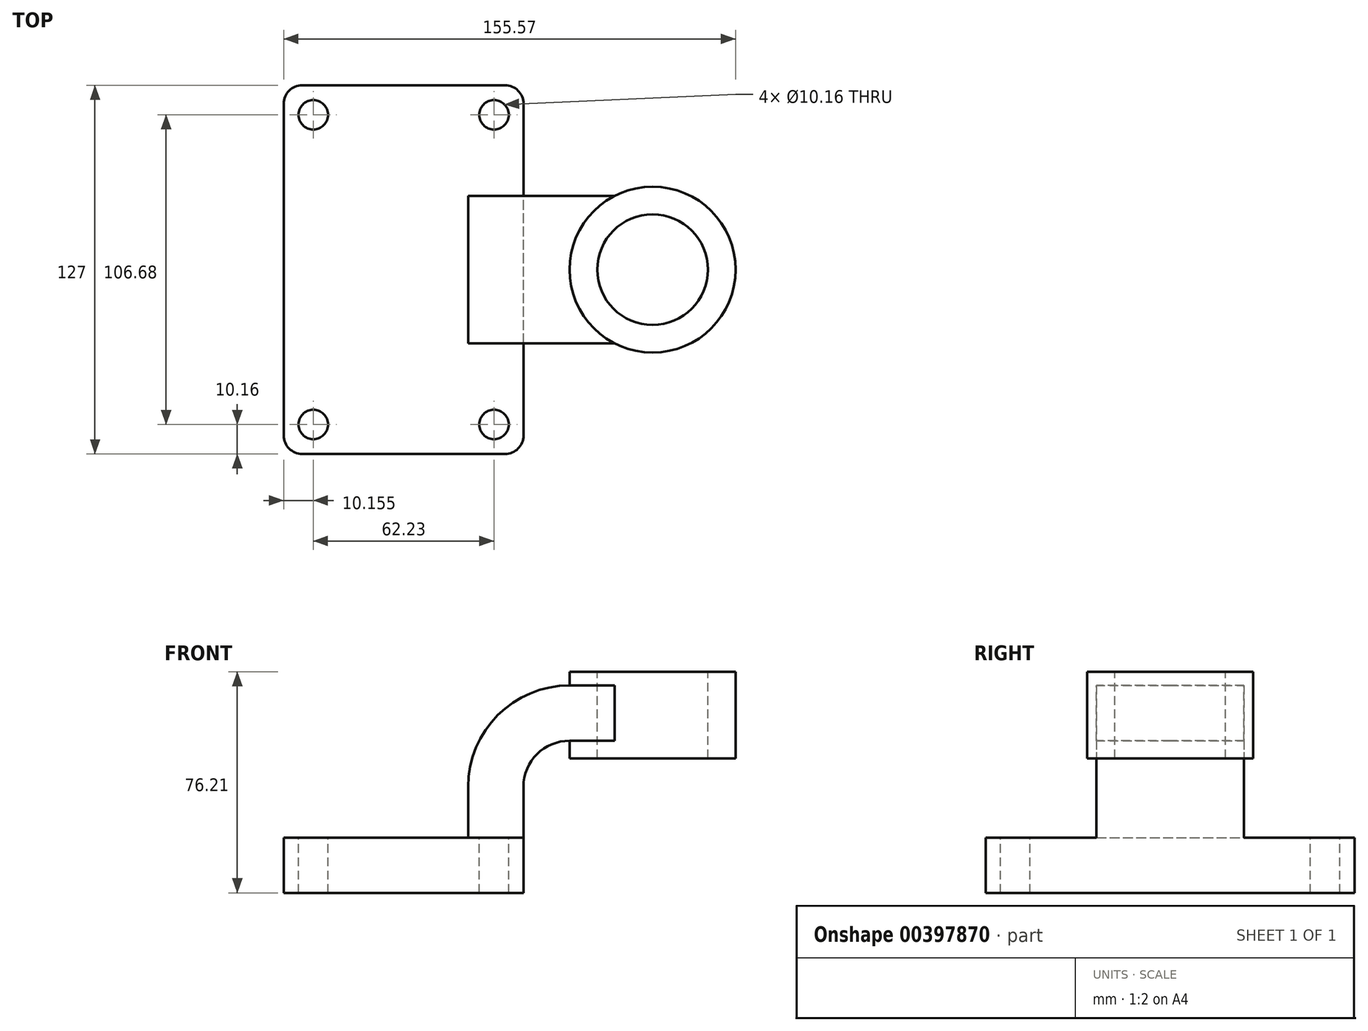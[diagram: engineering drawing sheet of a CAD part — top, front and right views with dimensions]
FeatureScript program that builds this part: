
annotation { "Feature Type Name" : "Feature", "Feature Type Description" : "" }
export const myFeature = defineFeature(function(context is Context, id is Id, definition is map)
    precondition{}
    {
        {
            var Q0;
            Q0=qCreatedBy(makeId("Front.planeOp"),FACE);
            var sketch = newSketch(context, id + "F0", { "sketchPlane" : qUnion([Q0])});
            skLineSegment(sketch, "E0.bottom", {"start": v(41.27, 9.53) * mm, "end": v(-41.28, 9.53) * mm});
            skLineSegment(sketch, "E0.top", {"start": v(41.28, -9.52) * mm, "end": v(-41.27, -9.52) * mm});
            skLineSegment(sketch, "E0.left", {"start": v(41.28, 9.53) * mm, "end": v(41.28, -9.52) * mm});
            skLineSegment(sketch, "E0.right", {"start": v(-41.28, 9.53) * mm, "end": v(-41.27, -9.52) * mm});
            skPoint(sketch, "E0.middle", {"position": v(0, 0) * mm});
            skLineSegment(sketch, "E1.bottom", {"start": v(114.3, 66.68) * mm, "end": v(57.15, 66.68) * mm});
            skLineSegment(sketch, "E1.top", {"start": v(114.3, 36.84) * mm, "end": v(57.15, 36.84) * mm});
            skLineSegment(sketch, "E1.left", {"start": v(114.3, 66.68) * mm, "end": v(114.3, 36.84) * mm});
            skLineSegment(sketch, "E1.right", {"start": v(57.15, 66.68) * mm, "end": v(57.15, 36.84) * mm});
            skPoint(sketch, "E1.middle", {"position": v(85.72, 51.76) * mm});
            skLineSegment(sketch, "E2", {"start": v(41.27, 9.53) * mm, "end": v(41.27, 27) * mm});
            skArc(sketch, "E3", {"start": v(41.27, 27) * mm, "mid": v(45.92, 38.23) * mm, "end": v(57.15, 42.88) * mm});
            skLineSegment(sketch, "E4", {"start": v(57.15, 42.88) * mm, "end": v(85.72, 42.88) * mm});
            skLineSegment(sketch, "E5.0", {"start": v(57.15, 61.93) * mm, "end": v(85.72, 61.93) * mm});
            skArc(sketch, "E5.1", {"start": v(22.23, 27) * mm, "mid": v(32.45, 51.7) * mm, "end": v(57.15, 61.93) * mm});
            skLineSegment(sketch, "E5.2", {"start": v(22.23, 9.53) * mm, "end": v(22.23, 27) * mm});
            skFitSpline(sketch, "E6", {"points": [v(-41.28, 9.53) * mm, v(57.15, 61.93) * mm], "startDerivative": vector(8.04, 87.02) * mm, "endDerivative": vector(125.87, -0.42) * mm});
            skLineSegment(sketch, "E7", {"start": v(85.72, 61.93) * mm, "end": v(85.72, 42.88) * mm});
            skLineSegment(sketch, "E8", {"start": v(85.72, 61.93) * mm, "end": v(85.72, 66.68) * mm});
            skLineSegment(sketch, "E9", {"start": v(85.72, 42.88) * mm, "end": v(85.72, 36.84) * mm});
            skSolve(sketch);
        }
        {
            var Q0;
            Q0=makeQuery(id+"F0.imprint","IMPRINT",FACE,{"disambiguationData":[TD([[makeQuery(id+"F0.imprint","IMPRINT",EDGE,{"derivedFrom":sQuery(id+"F0.wireOp",EDGE,"E0.top")}),-1.0]])]});
            extrude(context, id + "F1", {"entities" : qUnion([Q0]), "endBound" : BoundingType.SYMMETRIC, "depth" : 127 * mm});
        }
        {
            var Q0;
            {var subQ1=sQuery(id+"F0.wireOp",EDGE,"E2");Q0=makeQuery(id+"F0.imprint","IMPRINT",FACE,{"disambiguationData":[TD([[makeQuery(id+"F0.imprint","IMPRINT",EDGE,{"derivedFrom":subQ1}),1.0]])]});}
            var Q1;
            {var subQ5=sQuery(id+"F0.wireOp",EDGE,"E7");Q1=makeQuery(id+"F0.imprint","IMPRINT",FACE,{"disambiguationData":[TD([[makeQuery(id+"F0.imprint","IMPRINT",EDGE,{"derivedFrom":subQ5}),-1.0]])]});}
            extrude(context, id + "F2", {"entities" : qUnion([Q0, Q1]), "operationType" : NewBodyOperationType.ADD, "endBound" : BoundingType.SYMMETRIC, "depth" : 50.8 * mm});
        }
        {
            var Q0;
            Q0=makeQuery(id+"F0.imprint","IMPRINT",FACE,{"disambiguationData":[TD([[makeQuery(id+"F0.imprint","IMPRINT",EDGE,{"derivedFrom":sQuery(id+"F0.wireOp",EDGE,"E5.1")}),1.0]])]});
            extrude(context, id + "F3", {"entities" : qUnion([Q0]), "operationType" : NewBodyOperationType.ADD, "endBound" : BoundingType.SYMMETRIC, "depth" : 15.88 * mm});
        }
        {
            var Q0;
            {var subQ0=sQuery(id+"F0.wireOp",EDGE,"E1.left");Q0=makeQuery(id+"F0.imprint","IMPRINT",FACE,{"disambiguationData":[TD([[makeQuery(id+"F0.imprint","IMPRINT",EDGE,{"derivedFrom":subQ0}),-1.0]])]});}
            var Q1;
            Q1=sQuery(id+"F0.wireOp",EDGE,"E7");
            revolve(context, id + "F4", {"operationType" : NewBodyOperationType.ADD, "entities" : qUnion([Q0]), "axis" : qUnion([Q1]), "revolveType" : RevolveType.FULL});
        }
        {
            var Q0;
            Q0=makeQuery(id+"F1.opExtrude","CAP_EDGE",EDGE,{"disambiguationData":[OSD([sQuery(id+"F0.wireOp",EDGE,"E0.right")])],"isStart":false});
            var Q1;
            Q1=makeQuery(id+"F1.opExtrude","CAP_EDGE",EDGE,{"disambiguationData":[OSD([sQuery(id+"F0.wireOp",EDGE,"E0.left")])],"isStart":false});
            var Q2;
            Q2=makeQuery(id+"F1.opExtrude","CAP_EDGE",EDGE,{"disambiguationData":[OSD([sQuery(id+"F0.wireOp",EDGE,"E0.right")])],"isStart":true});
            var Q3;
            Q3=makeQuery(id+"F1.opExtrude","CAP_EDGE",EDGE,{"disambiguationData":[OSD([sQuery(id+"F0.wireOp",EDGE,"E0.left")])],"isStart":true});
            fillet(context, id + "F5", {"entities" : qUnion([Q0, Q1, Q2, Q3]), "radius" : 6.35 * mm, "tangentPropagation" : true, "allowEdgeOverflow" : false});
        }
        {
            var Q0;
            {var subQ3=sQuery(id+"F0.wireOp",EDGE,"E0.bottom");var subQ4=sQuery(id+"F0.wireOp",EDGE,"E0.right");var subQ5=sQuery(id+"F0.wireOp",EDGE,"E0.left");Q0=makeQuery(id+"F3.boolean.opBoolean","SPLIT",FACE,{"disambiguationData":[TD([makeQuery(id+"F1.opExtrude","CAP_FACE",FACE,{"disambiguationData":[OSD([subQ3,sQuery(id+"F0.wireOp",EDGE,"E0.top"),subQ5,subQ4])],"isStart":true})])],"derivedFrom":makeQuery(id+"F1.opExtrude","SWEPT_FACE",FACE,{"disambiguationData":[OSD([subQ3])]})});}
            var sketch = newSketch(context, id + "F6", { "sketchPlane" : qUnion([Q0])});
            skCircle(sketch, "E10", {"center": v(-31.12, 53.34) * mm, "radius": 5.08 * mm});
            skCircle(sketch, "E11", {"center": v(31.11, 53.34) * mm, "radius": 5.08 * mm});
            skCircle(sketch, "E12.MirrorC", {"center": v(-31.12, -53.34) * mm, "radius": 5.08 * mm});
            skCircle(sketch, "E13.MirrorC", {"center": v(31.11, -53.34) * mm, "radius": 5.08 * mm});
            skSolve(sketch);
        }
        {
            var Q0;
            Q0 = qSketchRegion(id + "F6", true);
            extrude(context, id + "F7", {"entities" : qUnion([Q0]), "operationType" : NewBodyOperationType.REMOVE, "oppositeDirection" : true, "depth" : 25.4 * mm});
        }
        {
            var Q0;
            Q0=makeQuery(id+"F4.opRevolve","SWEPT_FACE",FACE,{"disambiguationData":[OSD([sQuery(id+"F0.wireOp",EDGE,"E1.bottom")])]});
            var sketch = newSketch(context, id + "F8", { "sketchPlane" : qUnion([Q0])});
            skCircle(sketch, "E14", {"center": v(85.72, 0) * mm, "radius": 19.05 * mm});
            skSolve(sketch);
        }
        {
            var Q0;
            Q0 = qSketchRegion(id + "F8", true);
            extrude(context, id + "F9", {"entities" : qUnion([Q0]), "operationType" : NewBodyOperationType.REMOVE, "oppositeDirection" : true, "depth" : 36.83 * mm});
        }
    });
